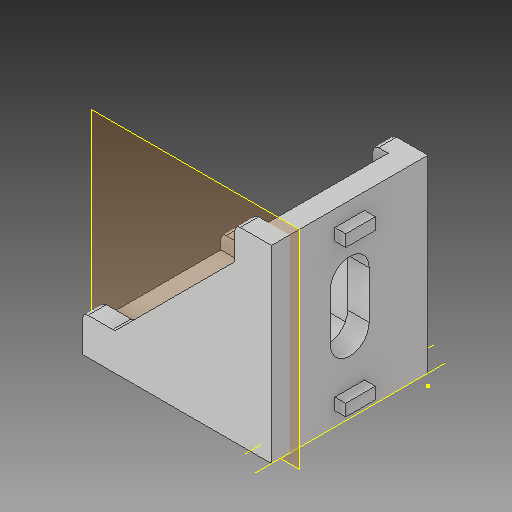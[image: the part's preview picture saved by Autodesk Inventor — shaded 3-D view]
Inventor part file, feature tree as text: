
AUTODESK INVENTOR PART (.ipt)
format: ipt  version: 2017 (Build 210142000, 142)  size: 179,712 bytes
history: native  units: mm
features: sketch x8, other x5, plane x1
ambient origin geometry x8: Origin, YZ Plane, XZ Plane, XY Plane, X Axis, Y Axis, Z Axis, Center Point
bodies: Solid1 (feature_tree)
feature tree (14):
  other  "30mm Bracket_CPY_MIR2_MIR_MIR.ipt"
  other  "Solid1::30mm Bracket_CPY_MIR2_MIR_MIR.ipt"
  other  "TaggingFeature1"
  sketch  "Sketch1"  dims[d0=10.0mm]
  sketch  "Sketch2"
  sketch  "Sketch3"
  sketch  "Sketch4"
  sketch  "Sketch5"
  sketch  "Sketch7"
  sketch  "Sketch9"
  sketch  "Sketch10"
  plane  "Work Plane1"
  other  "Work Axis1"
  other  "Work Axis2"
